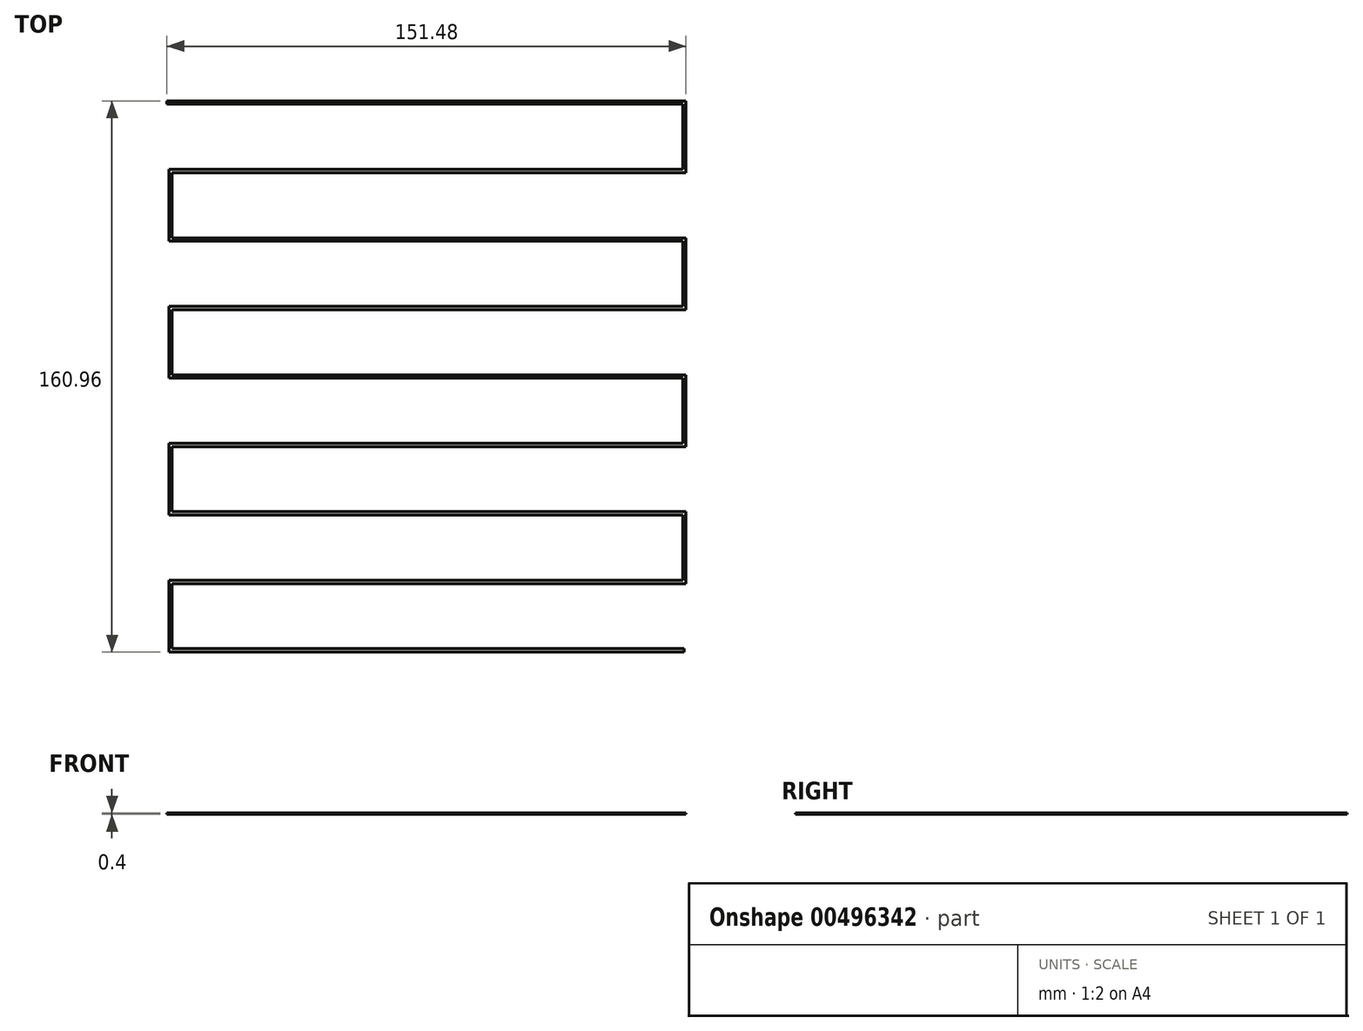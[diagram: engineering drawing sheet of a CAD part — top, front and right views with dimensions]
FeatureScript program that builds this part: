
annotation { "Feature Type Name" : "Feature", "Feature Type Description" : "" }
export const myFeature = defineFeature(function(context is Context, id is Id, definition is map)
    precondition{}
    {
        {
            assignVariable(context, id + "F0", {"name" : "trace_thickness", "anyValue" : .4});
        }
        {
            var Q0;
            Q0=qCreatedBy(makeId("Top.planeOp"),FACE);
            var sketch = newSketch(context, id + "F1", { "sketchPlane" : qUnion([Q0])});
            skLineSegment(sketch, "E0.bottom", {"start": v(125, 105) * mm, "end": v(-125, 105) * mm, "construction": true});
            skLineSegment(sketch, "E0.top", {"start": v(125, -105) * mm, "end": v(-125, -105) * mm, "construction": true});
            skLineSegment(sketch, "E0.left", {"start": v(125, 105) * mm, "end": v(125, -105) * mm, "construction": true});
            skLineSegment(sketch, "E0.right", {"start": v(-125, 105) * mm, "end": v(-125, -105) * mm, "construction": true});
            skPoint(sketch, "E0.middle", {"position": v(0, 0) * mm});
            skPoint(sketch, "E1", {"position": v(-125, 85) * mm});
            skPoint(sketch, "E2", {"position": v(-75, 105) * mm});
            skLineSegment(sketch, "E3", {"start": v(-75, 85) * mm, "end": v(75, 85) * mm});
            skLineSegment(sketch, "E4", {"start": v(75, 85) * mm, "end": v(75, 65) * mm});
            skLineSegment(sketch, "E5", {"start": v(75, 65) * mm, "end": v(-75, 65) * mm});
            skLineSegment(sketch, "E6", {"start": v(-75, 65) * mm, "end": v(-75, 45) * mm});
            skLineSegment(sketch, "E7", {"start": v(-75, 45) * mm, "end": v(75, 45) * mm});
            skLineSegment(sketch, "E8", {"start": v(75, 45) * mm, "end": v(75, 25) * mm});
            skLineSegment(sketch, "E9", {"start": v(75, 25) * mm, "end": v(-75, 25) * mm});
            skLineSegment(sketch, "E10", {"start": v(-75, 25) * mm, "end": v(-75, 5) * mm});
            skLineSegment(sketch, "E11", {"start": v(-75, 5) * mm, "end": v(75, 5) * mm});
            skLineSegment(sketch, "E12", {"start": v(75, 5) * mm, "end": v(75, -15) * mm});
            skLineSegment(sketch, "E13", {"start": v(75, -15) * mm, "end": v(-75, -15) * mm});
            skLineSegment(sketch, "E14", {"start": v(-75, -15) * mm, "end": v(-75, -35) * mm});
            skLineSegment(sketch, "E15", {"start": v(-75, -35) * mm, "end": v(75, -35) * mm});
            skLineSegment(sketch, "E16", {"start": v(75, -35) * mm, "end": v(75, -55) * mm});
            skLineSegment(sketch, "E17", {"start": v(75, -55) * mm, "end": v(-75, -55) * mm});
            skLineSegment(sketch, "E18", {"start": v(-75, -55) * mm, "end": v(-75, -75) * mm});
            skLineSegment(sketch, "E19", {"start": v(-75, -75) * mm, "end": v(75, -75) * mm});
            skLineSegment(sketch, "E20", {"start": v(-75, 85) * mm, "end": v(-75, 85.48) * mm});
            skLineSegment(sketch, "E21", {"start": v(-75, 85.48) * mm, "end": v(-76, 85.48) * mm});
            skLineSegment(sketch, "E22", {"start": v(-76, 85.48) * mm, "end": v(-76, 84.52) * mm});
            skLineSegment(sketch, "E23", {"start": v(-76, 84.52) * mm, "end": v(-75, 84.52) * mm});
            skLineSegment(sketch, "E24", {"start": v(-75, 84.52) * mm, "end": v(-75, 85) * mm});
            skSolve(sketch);
        }
        {
            var Q0;
            Q0=makeQuery(id+"F1.imprint","IMPRINT",FACE,{"disambiguationData":[TD([[makeQuery(id+"F1.imprint","IMPRINT",EDGE,{"derivedFrom":sQuery(id+"F1.wireOp",EDGE,"E20")}),1.0]])]});
            extrude(context, id + "F2", {"entities" : qUnion([Q0]), "depth" : (getVariable(context, 'trace_thickness')) * mm});
        }
        {
            var Q0;
            Q0=makeQuery(id+"F2.opExtrude","SWEPT_FACE",FACE,{"disambiguationData":[OSD([sQuery(id+"F1.wireOp",EDGE,"E20"),sQuery(id+"F1.wireOp",EDGE,"E24")])]});
            var Q1;
            Q1=sQuery(id+"F1.wireOp",EDGE,"E3");
            var Q2;
            Q2=sQuery(id+"F1.wireOp",EDGE,"E4");
            var Q3;
            Q3=sQuery(id+"F1.wireOp",EDGE,"E5");
            var Q4;
            Q4=sQuery(id+"F1.wireOp",EDGE,"E7");
            var Q5;
            Q5=sQuery(id+"F1.wireOp",EDGE,"E6");
            var Q6;
            Q6=sQuery(id+"F1.wireOp",EDGE,"E8");
            var Q7;
            Q7=sQuery(id+"F1.wireOp",EDGE,"E9");
            var Q8;
            Q8=sQuery(id+"F1.wireOp",EDGE,"E11");
            var Q9;
            Q9=sQuery(id+"F1.wireOp",EDGE,"E10");
            var Q10;
            Q10=sQuery(id+"F1.wireOp",EDGE,"E12");
            var Q11;
            Q11=sQuery(id+"F1.wireOp",EDGE,"E13");
            var Q12;
            Q12=sQuery(id+"F1.wireOp",EDGE,"E14");
            var Q13;
            Q13=sQuery(id+"F1.wireOp",EDGE,"E15");
            var Q14;
            Q14=sQuery(id+"F1.wireOp",EDGE,"E16");
            var Q15;
            Q15=sQuery(id+"F1.wireOp",EDGE,"E17");
            var Q16;
            Q16=sQuery(id+"F1.wireOp",EDGE,"E18");
            var Q17;
            Q17=sQuery(id+"F1.wireOp",EDGE,"E19");
            sweep(context, id + "F3", {"operationType" : NewBodyOperationType.ADD, "profiles" : qUnion([Q0]), "path" : qUnion([Q1, Q2, Q3, Q4, Q5, Q6, Q7, Q8, Q9, Q10, Q11, Q12, Q13, Q14, Q15, Q16, Q17])});
        }
    });
